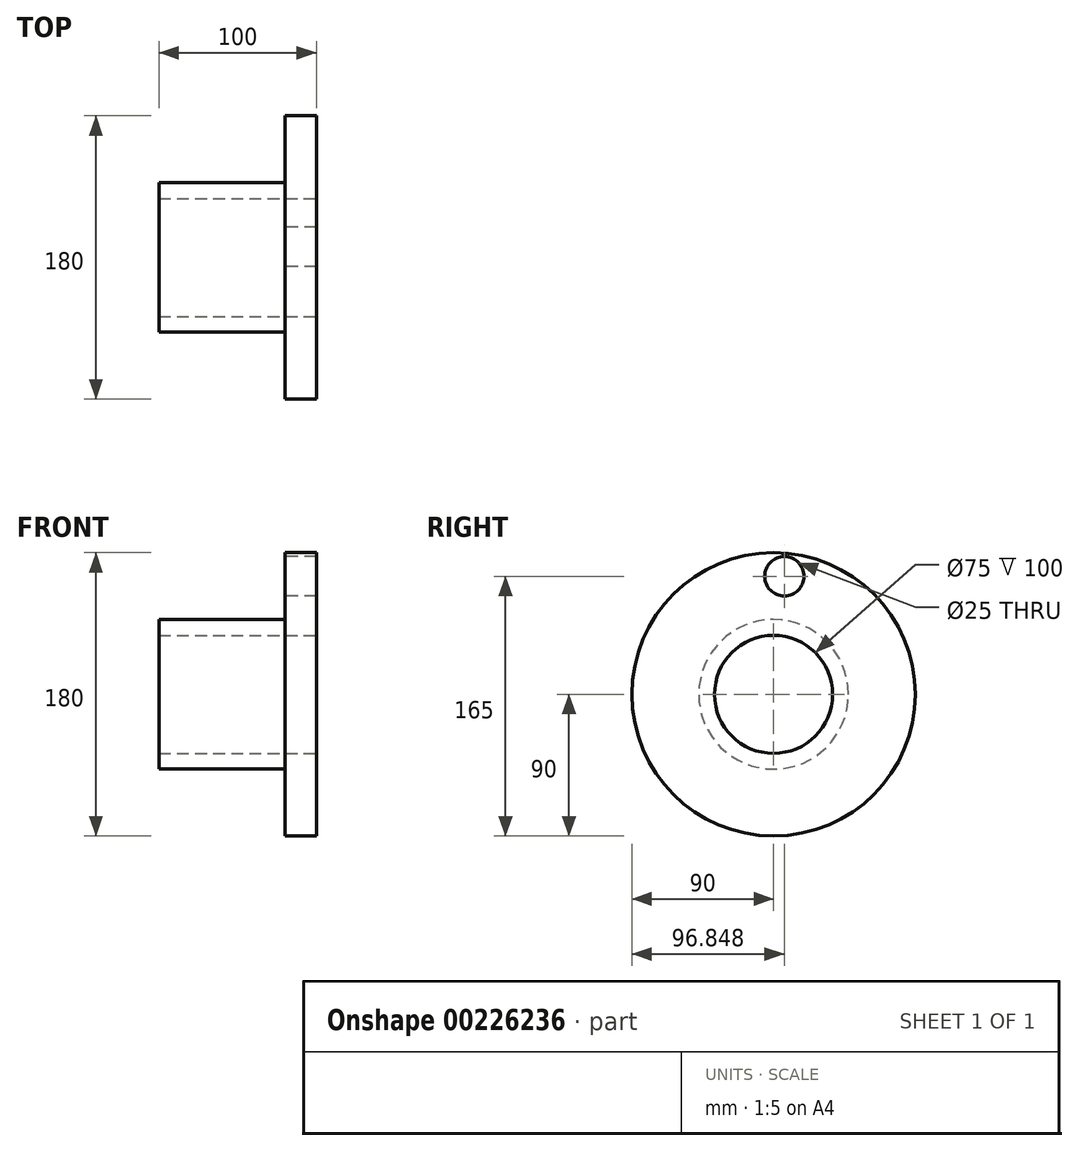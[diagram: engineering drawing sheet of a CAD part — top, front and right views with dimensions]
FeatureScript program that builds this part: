
annotation { "Feature Type Name" : "Feature", "Feature Type Description" : "" }
export const myFeature = defineFeature(function(context is Context, id is Id, definition is map)
    precondition{}
    {
        {
            var Q0;
            Q0=qCreatedBy(makeId("Front.planeOp"),FACE);
            var sketch = newSketch(context, id + "F0", { "sketchPlane" : qUnion([Q0])});
            skLineSegment(sketch, "E0", {"start": v(0, 0) * mm, "end": v(-335.77, 0) * mm, "construction": true});
            skLineSegment(sketch, "E1", {"start": v(0, 37.5) * mm, "end": v(0, 90) * mm});
            skLineSegment(sketch, "E2", {"start": v(0, 90) * mm, "end": v(-20, 90) * mm});
            skLineSegment(sketch, "E3", {"start": v(-20, 90) * mm, "end": v(-20, 47.5) * mm});
            skLineSegment(sketch, "E4", {"start": v(-20, 47.5) * mm, "end": v(-100, 47.5) * mm});
            skLineSegment(sketch, "E5", {"start": v(-100, 47.5) * mm, "end": v(-100, 37.5) * mm});
            skLineSegment(sketch, "E6", {"start": v(-100, 37.5) * mm, "end": v(0, 37.5) * mm});
            skSolve(sketch);
        }
        {
            var Q0;
            Q0=makeQuery(id+"F0.imprint","IMPRINT",FACE,{"disambiguationData":[TD([[makeQuery(id+"F0.imprint","IMPRINT",EDGE,{"derivedFrom":sQuery(id+"F0.wireOp",EDGE,"E1")}),1.0]])]});
            var Q1;
            Q1=sQuery(id+"F0.wireOp",EDGE,"E0");
            revolve(context, id + "F1", {"entities" : qUnion([Q0]), "axis" : qUnion([Q1]), "revolveType" : RevolveType.FULL});
        }
        {
            var Q0;
            Q0=makeQuery(id+"F1.opRevolve","SWEPT_FACE",FACE,{"disambiguationData":[OSD([sQuery(id+"F0.wireOp",EDGE,"E3")])]});
            var sketch = newSketch(context, id + "F2", { "sketchPlane" : qUnion([Q0])});
            skCircle(sketch, "E7", {"center": v(-6.85, 75) * mm, "radius": 12.5 * mm});
            skSolve(sketch);
        }
        {
            var Q0;
            Q0=makeQuery(id+"F2.imprint","IMPRINT",FACE,{"disambiguationData":[TD([[makeQuery(id+"F2.imprint","IMPRINT",EDGE,{"derivedFrom":sQuery(id+"F2.wireOp",EDGE,"E7")}),1.0]])]});
            extrude(context, id + "F3", {"entities" : qUnion([Q0]), "operationType" : NewBodyOperationType.REMOVE, "endBound" : BoundingType.THROUGH_ALL, "oppositeDirection" : true, "depth" : 25 * mm});
        }
    });
